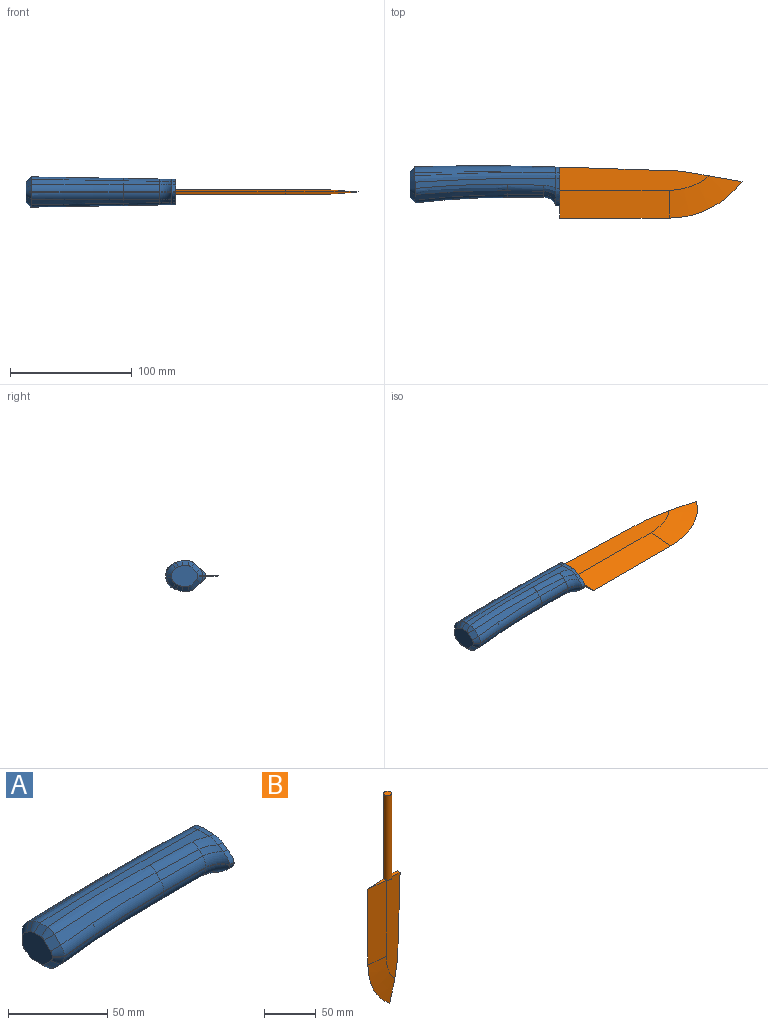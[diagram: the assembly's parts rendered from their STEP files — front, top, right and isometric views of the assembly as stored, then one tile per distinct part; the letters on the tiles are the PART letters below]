
ASSEMBLY  parts=2 mates=1
PART A: 64 faces, bbox 214.1x34.2x26.1 mm
  f0: cylinder r=1788.01mm len=116.06mm, axis (0,0,-1), area 221.2mm2, adj f19,f20,f34,f49
  f1: plane 21.49x16.75mm, normal (-1,0,0), area 283.1mm2, adj f46,f47,f48,f49,f50,f51,f52,f53
  f2: cylinder r=642.5mm len=75.45mm, axis (0,0,-1), area 28.2mm2, adj f3,f15,f18,f58
  f3: plane 30x0.37mm, normal (0,-1,0), area 11.2mm2, adj f2,f4,f14,f17
  f4: cylinder r=10.64mm len=10mm, axis (0,0,-1), area 4.8mm2, adj f3,f13,f16,f41
  f5: cone r=1788.01mm half-angle=60deg, axis (0,0,1), area 131.1mm2, adj f19,f29,f53
  f6: cone r=1778.01mm half-angle=60deg, axis (0,0,-1), area 131.1mm2, adj f20,f30,f46
  f7: cone r=19.64mm half-angle=45deg, axis (0,0,1), area 42.2mm2, adj f8,f13,f26,f39
  f8: plane 30x3.27mm, normal (0,-0.71,0.71), area 128.2mm2, adj f7,f9,f14,f27
  f9: cone r=642.5mm half-angle=45deg, axis (0,0,1), area 418.7mm2, adj f8,f15,f28,f54
  f10: cone r=10.64mm half-angle=45deg, axis (0,0,-1), area 42.2mm2, adj f11,f16,f23,f43
  f11: plane 30x3.27mm, normal (0,-0.71,-0.71), area 128.2mm2, adj f10,f12,f17,f24
  f12: cone r=651.5mm half-angle=45deg, axis (0,0,-1), area 418.7mm2, adj f11,f18,f25,f61
  f13: torus R=18.64mm, axis (0,0,-1), area 75.1mm2, adj f4,f7,f14,f40
  f14: cylinder r=8mm len=30mm, axis (1,0,0), area 188.5mm2, adj f3,f8,f13,f15
  f15: torus R=650.5mm, axis (0,0,-1), area 475.4mm2, adj f2,f9,f14,f56
  f16: torus R=18.64mm, axis (0,0,1), area 75.1mm2, adj f4,f10,f17,f42
  f17: cylinder r=8mm len=30mm, axis (1,0,0), area 188.5mm2, adj f3,f11,f16,f18
  f18: torus R=650.5mm, axis (0,0,1), area 475.4mm2, adj f2,f12,f17,f60
  f19: torus R=1778.01mm, axis (0,0,-1), area 1209.6mm2, adj f0,f5,f29,f33,f51
  f20: torus R=1778.01mm, axis (0,0,1), area 1209.6mm2, adj f0,f6,f30,f35,f47
  f21: plane 115.86x8.44mm, normal (0.02,0,1), area 576.1mm2, adj f26,f27,f28,f30,f37,f50
  f22: plane 115.86x8.44mm, normal (0.02,0,-1), area 576.1mm2, adj f23,f24,f25,f29,f31,f57
  f23: bspline ~13.3x8.82mm, area 59.3mm2, adj f10,f22,f24,f44
  f24: cylinder r=7mm len=30.12mm, axis (-1,0.02,-0.02), area 165mm2, adj f11,f22,f23,f25
  f25: bspline ~76.17x8.19mm, area 416.8mm2, adj f12,f22,f24,f59
  f26: bspline ~13.3x8.82mm, area 59.3mm2, adj f7,f21,f27,f38
  f27: cylinder r=7mm len=30.12mm, axis (1,-0.02,-0.02), area 165mm2, adj f8,f21,f26,f28
  f28: bspline ~76.17x8.19mm, area 416.8mm2, adj f9,f21,f27,f52
  f29: bspline ~213.86x10.07mm, area 601.6mm2, adj f5,f19,f22,f32,f55
  f30: bspline ~213.86x10.07mm, area 601.6mm2, adj f6,f20,f21,f36,f48
  f31: plane 8.42x3mm, normal (0,0,-1), area 25.2mm2, adj f22,f32,f44,f45
  f32: extruded ~4.6x3mm, area 14.3mm2, adj f29,f31,f33,f45
  f33: extruded ~8.43x4.62mm, area 30.1mm2, adj f19,f32,f34,f45
  f34: plane 3x1.91mm, normal (0,1,0), area 5.7mm2, adj f0,f33,f35,f45
  f35: extruded ~8.43x4.62mm, area 30.1mm2, adj f20,f34,f36,f45
  f36: extruded ~4.6x3mm, area 14.3mm2, adj f30,f35,f37,f45
  f37: plane 8.42x3mm, normal (0,0,1), area 25.2mm2, adj f21,f36,f38,f45
  f38: extruded ~6.12x3mm, area 19.7mm2, adj f26,f37,f39,f45
  f39: extruded ~3.61x3mm, area 13.3mm2, adj f7,f38,f40,f45
  f40: extruded ~5.66x4.64mm, area 22.7mm2, adj f13,f39,f41,f45
  f41: plane 3x0.37mm, normal (0,-1,0), area 1.1mm2, adj f4,f40,f42,f45
  f42: extruded ~5.66x4.64mm, area 22.7mm2, adj f16,f41,f43,f45
  f43: extruded ~3.61x3mm, area 13.3mm2, adj f10,f42,f44,f45
  f44: extruded ~6.12x3mm, area 19.7mm2, adj f23,f31,f43,f45
  f45: plane 32.26x21.26mm, normal (1,0,0), area 490.4mm2, adj f31,f32,f33,f34,f35,f36,f37,f38
  f46: bspline ~5x4.59mm, area 16.9mm2, adj f1,f6,f47,f48
  f47: bspline ~8.66x7.04mm, area 47.4mm2, adj f1,f20,f46,f49
  f48: bspline ~5.01x4.86mm, area 24.1mm2, adj f1,f30,f46,f50
  f49: plane 4.07x3.94mm, normal (-0.72,0.7,0), area 10.8mm2, adj f0,f1,f47,f51
  f50: plane 5.16x4.14mm, normal (-0.7,0,0.71), area 29.9mm2, adj f1,f21,f48,f52
  f51: bspline ~8.66x7.04mm, area 47.4mm2, adj f1,f19,f49,f53
  f52: bspline ~4.94x4.92mm, area 23mm2, adj f1,f28,f50,f54
  f53: bspline ~5x4.59mm, area 16.9mm2, adj f1,f5,f51,f55
  f54: bspline ~7.43x7.42mm, area 38.6mm2, adj f1,f9,f52,f56
  f55: bspline ~5.01x4.87mm, area 24.1mm2, adj f1,f29,f53,f57
  f56: bspline ~5.66x5.21mm, area 28.4mm2, adj f1,f15,f54,f58
  f57: plane 5.16x4.14mm, normal (-0.7,0,-0.71), area 29.9mm2, adj f1,f22,f55,f59
  f58: plane 4.55x4.04mm, normal (-0.66,-0.75,0), area 2.3mm2, adj f1,f2,f56,f60
  f59: bspline ~4.94x4.92mm, area 23mm2, adj f1,f25,f57,f61
  f60: bspline ~5.66x5.21mm, area 28.4mm2, adj f1,f18,f58,f61
  f61: bspline ~7.43x7.42mm, area 38.6mm2, adj f1,f12,f59,f60
  f62: cone r=0mm half-angle=59deg, axis (1,0,0), area 58.6mm2, adj f63
  f63: cylinder r=4mm len=50mm, axis (1,0,0), area 1256.6mm2, adj f45,f62
PART B: 14 faces, bbox 43.7x8x249.9 mm
  f0: plane 6.93x2mm, normal (0,0,-1), area 9.8mm2, adj f1,f6
  f1: cylinder r=4mm len=100mm, axis (0,0,-1), area 2513.3mm2, adj f0,f2,f3,f4,f7
  f2: plane 8x8mm, normal (0,0,1), area 50.3mm2, adj f1
  f3: plane 6.93x2mm, normal (0,0,-1), area 9.8mm2, adj f1,f5
  f4: plane 23.54x4mm, normal (0,0,1), area 47mm2, adj f1,f5,f6,f12,f13
  f5: plane 122.96x19.14mm, normal (0,-1,0), area 1938.6mm2, adj f3,f4,f7,f8,f9,f11,f13
  f6: plane 122.96x19.14mm, normal (0,1,0), area 1938.6mm2, adj f0,f4,f7,f8,f9,f10,f12
  f7: plane 11.54x4mm, normal (0,0,1), area 44.7mm2, adj f1,f5,f6,f8
  f8: plane 100.03x4mm, normal (1,0,-0.03), area 400.3mm2, adj f5,f6,f7,f9
  f9: plane 49.88x8.67mm, normal (0.99,0,-0.17), area 149.2mm2, adj f5,f6,f8,f10,f11
  f10: cone r=74.88mm half-angle=85deg, axis (0,-1,0), area 1210.9mm2, adj f6,f9,f11,f12
  f11: cone r=52.02mm half-angle=85deg, axis (0,1,0), area 1210.9mm2, adj f5,f9,f10,f13
  f12: plane 90x22.86mm, normal (-0.09,1,0), area 2065.3mm2, adj f4,f6,f10,f13
  f13: plane 90x22.86mm, normal (-0.09,-1,0), area 2065.3mm2, adj f4,f5,f11,f12
PLACE A t=(-46.54,19.8,-19.02)mm
PLACE B rot(axis=(-0.58,-0.58,0.58),120deg) t=(76.46,4.8,-6.52)mm
MATE fastened B.f1 <-> A.f62  axis (1,0,0) through (76.46,4.8,-6.52)mm
